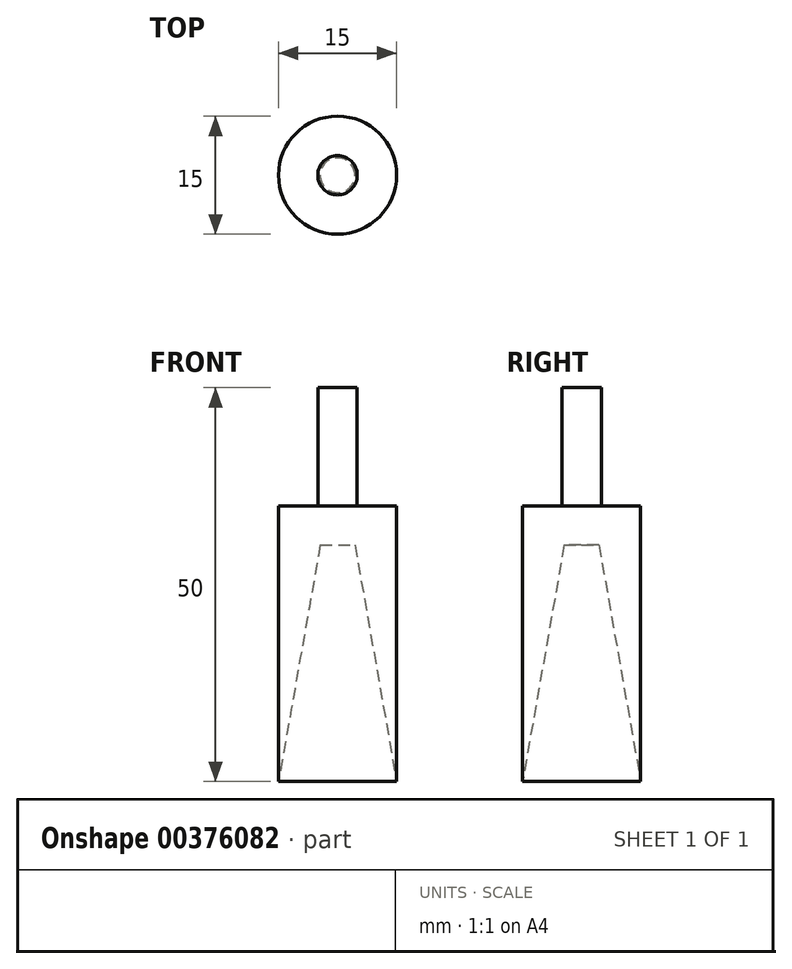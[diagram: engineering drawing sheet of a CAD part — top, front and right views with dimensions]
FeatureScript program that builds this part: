
annotation { "Feature Type Name" : "Feature", "Feature Type Description" : "" }
export const myFeature = defineFeature(function(context is Context, id is Id, definition is map)
    precondition{}
    {
        {
            var Q0;
            Q0=qCreatedBy(makeId("Top.planeOp"),FACE);
            var sketch = newSketch(context, id + "F0", { "sketchPlane" : qUnion([Q0])});
            skCircle(sketch, "E0", {"center": v(-41.05, 39.08) * mm, "radius": 7.5 * mm});
            skSolve(sketch);
        }
        {
            var Q0;
            Q0=makeQuery(id+"F0.imprint","IMPRINT",FACE,{"disambiguationData":[TD([[makeQuery(id+"F0.imprint","IMPRINT",EDGE,{"derivedFrom":sQuery(id+"F0.wireOp",EDGE,"E0")}),1.0]])]});
            extrude(context, id + "F1", {"entities" : qUnion([Q0]), "depth" : 50 * mm});
        }
        {
            var Q0;
            Q0=makeQuery(id+"F1.opExtrude","CAP_FACE",FACE,{"disambiguationData":[OSD([sQuery(id+"F0.wireOp",EDGE,"E0")])],"isStart":true});
            var sketch = newSketch(context, id + "F2", { "sketchPlane" : qUnion([Q0])});
            skCircle(sketch, "E1", {"center": v(-41.05, -39.08) * mm, "radius": 7.5 * mm});
            skSolve(sketch);
        }
        {
            var Q0;
            Q0 = qSketchRegion(id + "F2", true);
            extrude(context, id + "F3", {"entities" : qUnion([Q0]), "operationType" : NewBodyOperationType.REMOVE, "oppositeDirection" : true, "depth" : 30 * mm, "hasDraft" : true, "draftAngle" : 10 * degree, "draftPullDirection" : true});
        }
        {
            var Q0;
            Q0=makeQuery(id+"F1.opExtrude","CAP_FACE",FACE,{"disambiguationData":[OSD([sQuery(id+"F0.wireOp",EDGE,"E0")])],"isStart":false});
            var sketch = newSketch(context, id + "F4", { "sketchPlane" : qUnion([Q0])});
            skCircle(sketch, "E2", {"center": v(-41.05, 39.08) * mm, "radius": 7.5 * mm});
            skCircle(sketch, "E3", {"center": v(-41.05, 39.08) * mm, "radius": 2.5 * mm});
            skSolve(sketch);
        }
        {
            var Q0;
            Q0 = qSketchRegion(id + "F4", true);
            extrude(context, id + "F5", {"entities" : qUnion([Q0]), "operationType" : NewBodyOperationType.REMOVE, "oppositeDirection" : true, "depth" : 15 * mm});
        }
    });
